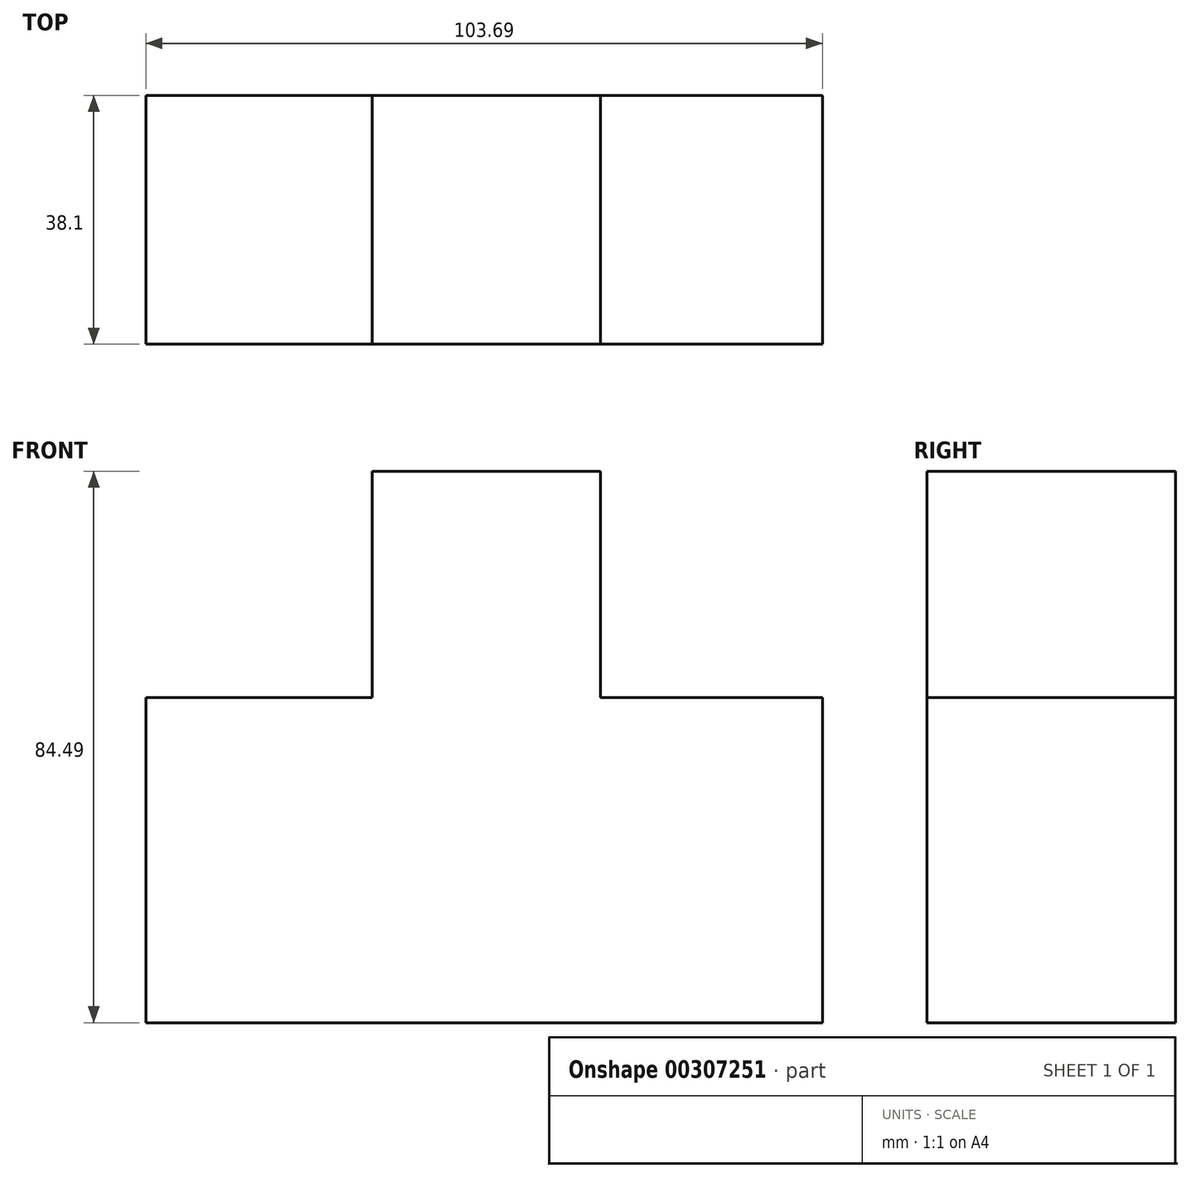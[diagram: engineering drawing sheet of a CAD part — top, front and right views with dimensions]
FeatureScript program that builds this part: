
annotation { "Feature Type Name" : "Feature", "Feature Type Description" : "" }
export const myFeature = defineFeature(function(context is Context, id is Id, definition is map)
    precondition{}
    {
        {
            var Q0;
            Q0=qCreatedBy(makeId("Front.planeOp"),FACE);
            var sketch = newSketch(context, id + "F0", { "sketchPlane" : qUnion([Q0])});
            skLineSegment(sketch, "E0", {"start": v(-47.05, -45.34) * mm, "end": v(56.64, -45.34) * mm});
            skLineSegment(sketch, "E1", {"start": v(56.64, -45.34) * mm, "end": v(56.64, 4.49) * mm});
            skLineSegment(sketch, "E2", {"start": v(-47.05, 4.49) * mm, "end": v(-47.05, -45.34) * mm});
            skLineSegment(sketch, "E3", {"start": v(-47.05, 4.49) * mm, "end": v(-12.38, 4.49) * mm});
            skLineSegment(sketch, "E4", {"start": v(-12.38, 4.49) * mm, "end": v(-12.38, 39.15) * mm});
            skLineSegment(sketch, "E5", {"start": v(56.64, 4.49) * mm, "end": v(22.6, 4.49) * mm});
            skLineSegment(sketch, "E6", {"start": v(22.6, 4.49) * mm, "end": v(22.6, 39.15) * mm});
            skLineSegment(sketch, "E7", {"start": v(22.6, 39.15) * mm, "end": v(-12.38, 39.15) * mm});
            skSolve(sketch);
        }
        {
            var Q0;
            Q0=makeQuery(id+"F0.imprint","IMPRINT",FACE,{"disambiguationData":[TD([[makeQuery(id+"F0.imprint","IMPRINT",EDGE,{"derivedFrom":sQuery(id+"F0.wireOp",EDGE,"E0")}),1.0]])]});
            extrude(context, id + "F1", {"entities" : qUnion([Q0]), "depth" : 38.1 * mm});
        }
    });
